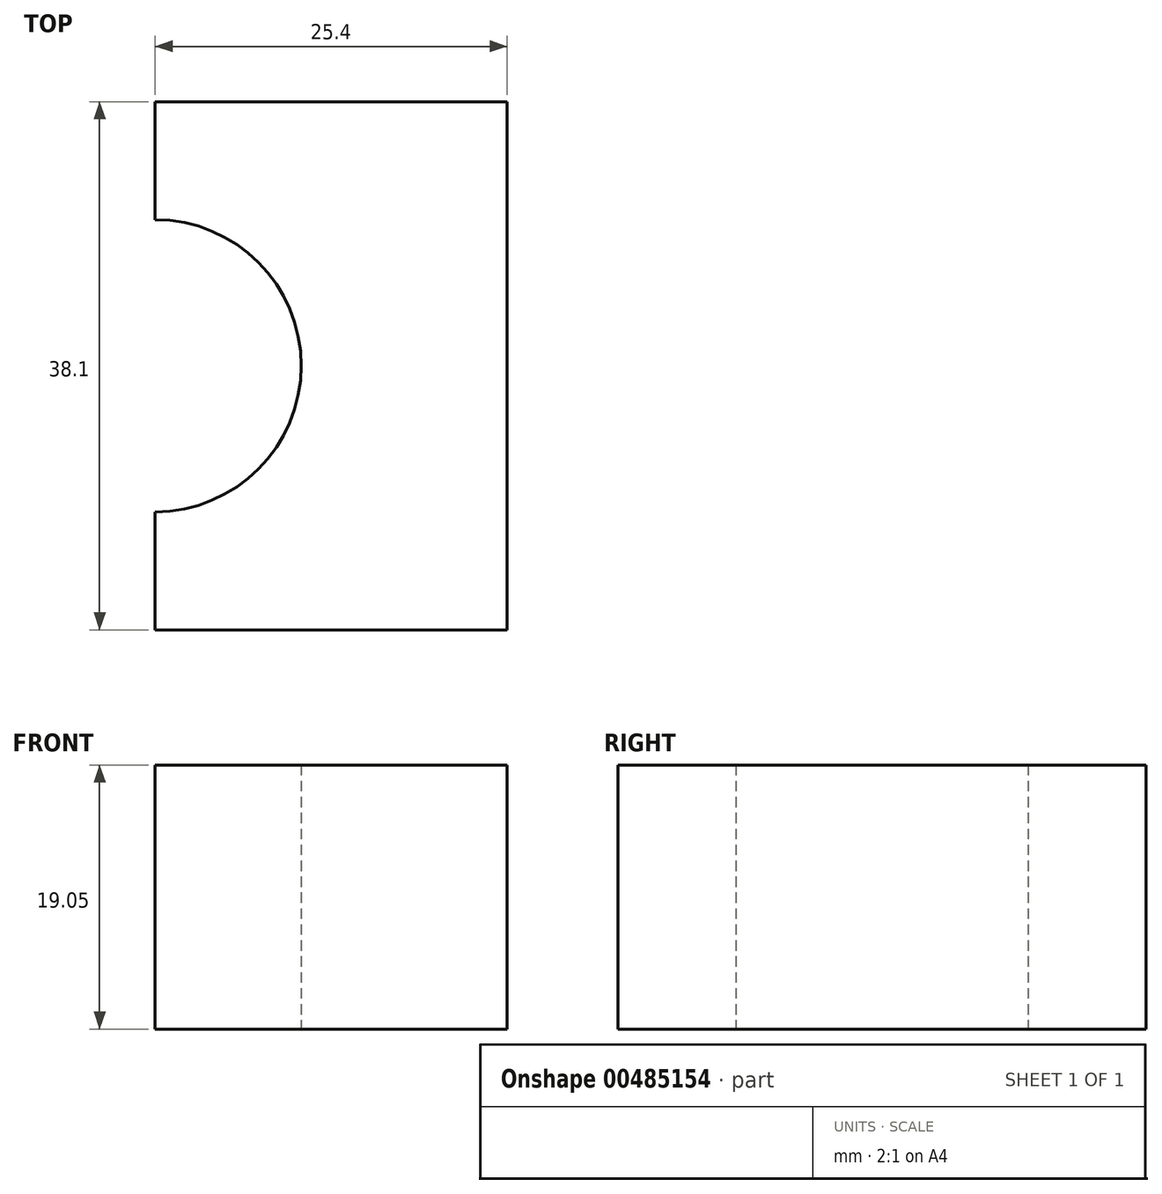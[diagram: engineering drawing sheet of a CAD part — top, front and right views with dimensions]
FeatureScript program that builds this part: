
annotation { "Feature Type Name" : "Feature", "Feature Type Description" : "" }
export const myFeature = defineFeature(function(context is Context, id is Id, definition is map)
    precondition{}
    {
        {
            var Q0;
            Q0=qCreatedBy(makeId("Top.planeOp"),FACE);
            var sketch = newSketch(context, id + "F0", { "sketchPlane" : qUnion([Q0])});
            skLineSegment(sketch, "E0.bottom", {"start": v(12.7, 19.05) * mm, "end": v(-12.7, 19.05) * mm});
            skLineSegment(sketch, "E0.top", {"start": v(12.7, -19.05) * mm, "end": v(-12.7, -19.05) * mm});
            skLineSegment(sketch, "E0.left", {"start": v(12.7, 19.05) * mm, "end": v(12.7, -19.05) * mm});
            skLineSegment(sketch, "E0.right", {"start": v(-12.7, 19.05) * mm, "end": v(-12.7, -19.05) * mm});
            skPoint(sketch, "E0.middle", {"position": v(0, 0) * mm});
            skCircle(sketch, "E1", {"center": v(-12.7, 0) * mm, "radius": 10.54 * mm});
            skSolve(sketch);
        }
        {
            var Q0;
            {var subQ1=sQuery(id+"F0.wireOp",EDGE,"E0.bottom");Q0=makeQuery(id+"F0.imprint","IMPRINT",FACE,{"disambiguationData":[TD([[makeQuery(id+"F0.imprint","IMPRINT",EDGE,{"derivedFrom":subQ1}),1.0]])]});}
            extrude(context, id + "F1", {"entities" : qUnion([Q0]), "depth" : 19.05 * mm});
        }
    });
